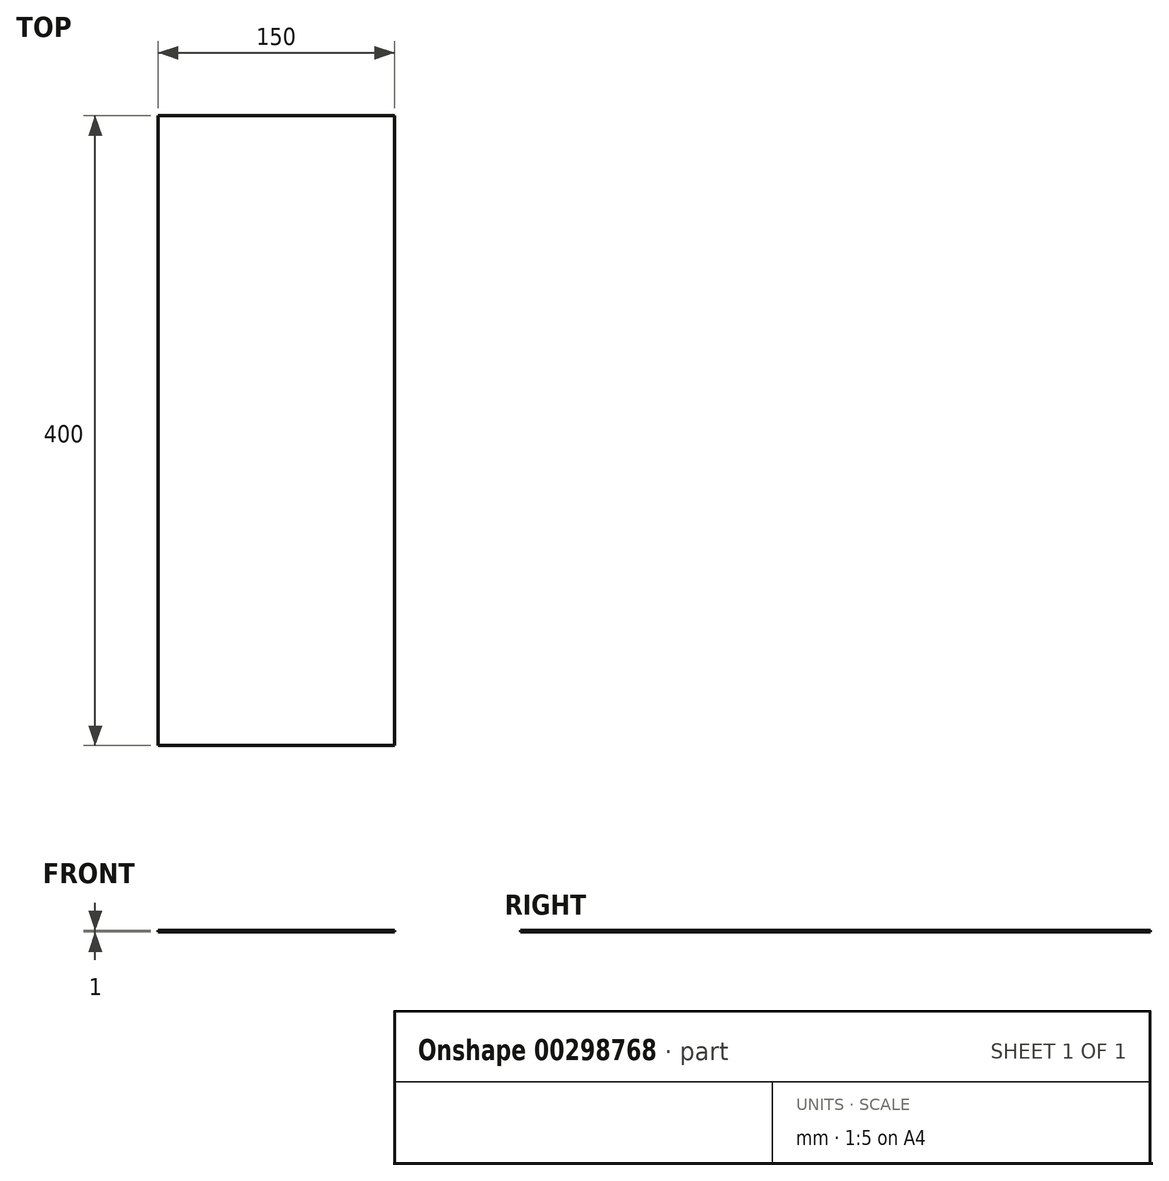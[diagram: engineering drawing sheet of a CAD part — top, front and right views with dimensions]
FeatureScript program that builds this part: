
annotation { "Feature Type Name" : "Feature", "Feature Type Description" : "" }
export const myFeature = defineFeature(function(context is Context, id is Id, definition is map)
    precondition{}
    {
        {
            var Q0;
            Q0=qCreatedBy(makeId("Top.planeOp"),FACE);
            var sketch = newSketch(context, id + "F0", { "sketchPlane" : qUnion([Q0])});
            skLineSegment(sketch, "E0.bottom", {"start": v(0, 400) * mm, "end": v(150, 400) * mm});
            skLineSegment(sketch, "E0.top", {"start": v(0, 0) * mm, "end": v(150, 0) * mm});
            skLineSegment(sketch, "E0.left", {"start": v(0, 400) * mm, "end": v(0, 0) * mm});
            skLineSegment(sketch, "E0.right", {"start": v(150, 400) * mm, "end": v(150, 0) * mm});
            skSolve(sketch);
        }
        {
            var Q0;
            Q0=makeQuery(id+"F0.imprint","IMPRINT",FACE,{"disambiguationData":[TD([[makeQuery(id+"F0.imprint","IMPRINT",EDGE,{"derivedFrom":sQuery(id+"F0.wireOp",EDGE,"E0.bottom")}),-1.0]])]});
            extrude(context, id + "F1", {"entities" : qUnion([Q0]), "depth" : 1 * mm});
        }
        {
            var Q0;
            Q0=makeQuery(id+"F1.opExtrude","SWEPT_BODY",BODY,{"disambiguationData":[OSD([sQuery(id+"F0.wireOp",EDGE,"E0.bottom"),sQuery(id+"F0.wireOp",EDGE,"E0.top"),sQuery(id+"F0.wireOp",EDGE,"E0.left"),sQuery(id+"F0.wireOp",EDGE,"E0.right")])]});
            transform(context, id + "F2", {"entities" : qUnion([Q0]), "transformType" : TransformType.TRANSLATION_3D, "dx" : -18 * mm, "dy" : -511 * mm, "dz" : 500 * mm, "makeCopy" : false});
        }
        {
            var Q0;
            Q0=makeQuery(id+"F1.opExtrude","SWEPT_BODY",BODY,{"disambiguationData":[OSD([sQuery(id+"F0.wireOp",EDGE,"E0.bottom"),sQuery(id+"F0.wireOp",EDGE,"E0.top"),sQuery(id+"F0.wireOp",EDGE,"E0.left"),sQuery(id+"F0.wireOp",EDGE,"E0.right")])]});
            transform(context, id + "F3", {"entities" : qUnion([Q0]), "transformType" : TransformType.TRANSLATION_3D, "dx" : -2.5 * mm, "dy" : 3.5 * mm, "dz" : 0 * mm, "makeCopy" : false});
        }
    });
